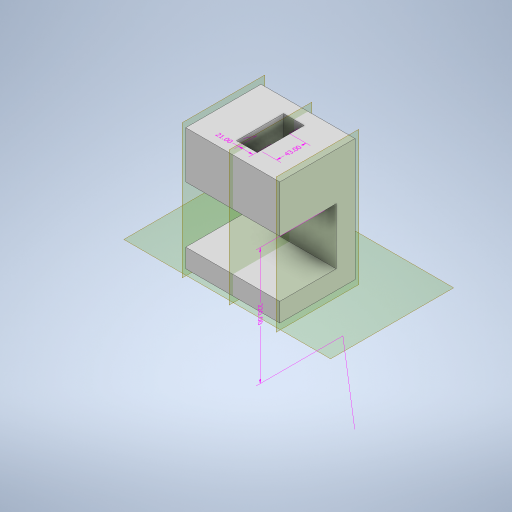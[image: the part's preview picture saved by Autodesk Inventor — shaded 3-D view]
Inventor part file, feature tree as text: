
AUTODESK INVENTOR PART (.ipt)
format: ipt  version: 2023 (Build 270158000, 158)  size: 340,480 bytes
history: native  units: mm
features: other x7, extrude x6, plane x6, sketch x6, split x3
ambient origin geometry x8: Origin, YZ Plane, XZ Plane, XY Plane, X Axis, Y Axis, Z Axis, Center Point
bodies: Body1 (feature_tree), Body2 (feature_tree)
feature tree (28):
  other  "Sólido1"
  other  "Anotaciones"
  extrude  "Extrusión1"  Depth=80.0mm
  extrude  "Extrusión2"  Depth=130.0mm
  extrude  "Extrusión3"  Depth=20.0mm
  extrude  "Extrusión4"  Depth=43.0mm TaperAngle=0.0deg
  plane  "Plano de trabajo1"
  extrude  "Extrusión6"  Depth=20.0mm TaperAngle=0.0deg
  plane  "Plano de trabajo3"
  extrude  "Extrusión7"  Depth=43.0mm TaperAngle=0.0deg
  plane  "Plano de trabajo4"
  split  "Dividir1"
  other  "Suprimir cara4"
  plane  "Plano de trabajo5"
  plane  "Plano de trabajo6"
  plane  "Plano de trabajo7"
  split  "Dividir2"
  split  "Dividir3"
  sketch  "Boceto1"  dims[d0=200.0mm d1=80.0mm]
  sketch  "Boceto2"  dims[d2=130.0mm d3=0.0mm d4=180.0mm]
  sketch  "Boceto3"  dims[d5=60.0mm d6=20.0mm]
  sketch  "Boceto4"  dims[d7=60.0mm d8=0.0mm d11=43.0mm d12=0.0mm]
  sketch  "Boceto7"  dims[d13=20.0mm d14=90.0mm d15=0.0mm]
  other  "Sólido3"
  sketch  "Boceto10"  dims[d16=-90.0mm d28=20.0mm d29=20.0mm d30=30.0mm d31=30.0mm d32=20.0mm d33=35.0mm d34=35.0mm d35=69.0mm d36=10.0mm d37=0.0mm d45=1.5mm d50=10.0mm d51=0.0mm d52=10.0mm d54=90.0deg d62=22.0mm d63=50.0mm d38=3.166395mm d39=4.283575mm d40=220.0mm d55=6.676554mm d56=4.512619mm d57=21.0mm d58=4.838905mm d59=6.893242mm d60=43.0mm]
  other  "Cota lineal 1"
  other  "Cota lineal 2"
  other  "Cota lineal 3"
